# Revit family: Comax
name_source: partatom
category: Structural Stiffeners
revit_build: Autodesk Revit 2018 (Build: 20170223_1515(x64)
units: mm (PartAtom-declared; Revit-internal decimal feet)

## family parameters
Cut with Voids When Loaded = Yes
Host = Face
Shared = No

## types (1)
- Comax
    # = 4
    #_acier_Down = 8
    #_acier_up = 9
    Default Elevation = 0 mm  [stored 0 ft]
    Hauteur_Acier = 30 mm  [stored 0.0984252 ft]
    L = 1250 mm  [stored 4.10105 ft]
    URL = www.rduarte.com
    a = 90 mm  [stored 0.295276 ft]
    a_aux = 78 mm  [stored 0.255906 ft]
    b = 120 mm  [stored 0.393701 ft]
    b_aux = 84 mm
    e = 150 mm
    lb = 500 mm  [stored 1.64042 ft]
    lb_aux = 530 mm
    p = 110 mm  [stored 0.360892 ft]
    s_aux = 650 mm  [stored 2.13255 ft]
    w = 150 mm
    w_aux = 150 mm
    Épaisseur_Acier = 3 mm  [stored 0.00984252 ft]
    Ø = 12 mm  [stored 0.0393701 ft]

note: [stored X ft] marks values corroborated as IEEE doubles in the binary element streams (Revit-internal decimal feet)

## geometry (parser evidence)
native form markers: Sweep x4
no freeform markers — native parametric forms only
